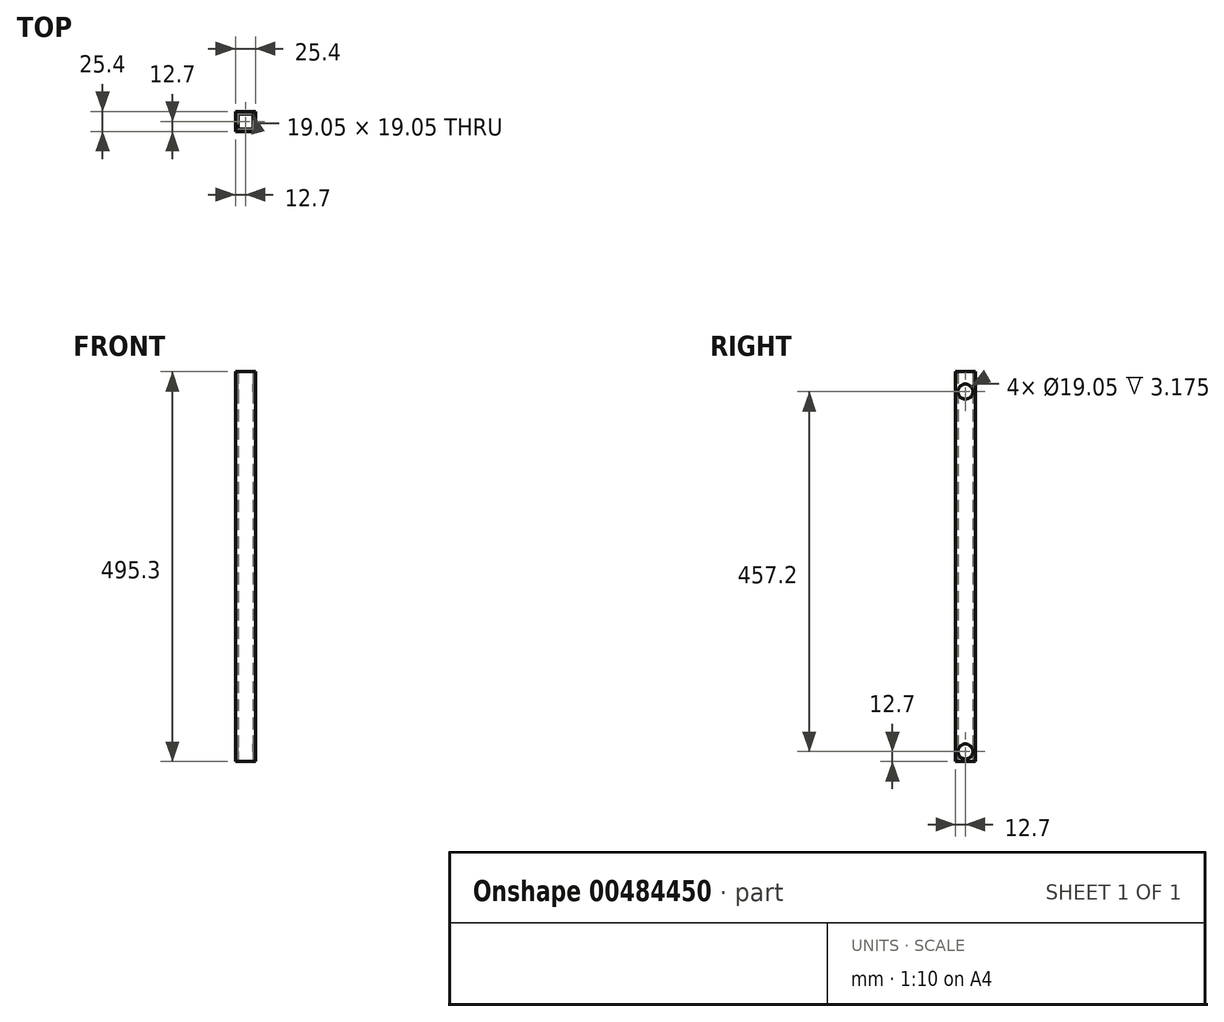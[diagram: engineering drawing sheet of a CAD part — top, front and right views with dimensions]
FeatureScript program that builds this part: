
annotation { "Feature Type Name" : "Feature", "Feature Type Description" : "" }
export const myFeature = defineFeature(function(context is Context, id is Id, definition is map)
    precondition{}
    {
        {
            var Q0;
            Q0=qCreatedBy(makeId("Top.planeOp"),FACE);
            var sketch = newSketch(context, id + "F0", { "sketchPlane" : qUnion([Q0])});
            skLineSegment(sketch, "E0.bottom", {"start": v(12.7, 12.7) * mm, "end": v(-12.7, 12.7) * mm});
            skLineSegment(sketch, "E0.top", {"start": v(12.7, -12.7) * mm, "end": v(-12.7, -12.7) * mm});
            skLineSegment(sketch, "E0.left", {"start": v(12.7, 12.7) * mm, "end": v(12.7, -12.7) * mm});
            skLineSegment(sketch, "E0.right", {"start": v(-12.7, 12.7) * mm, "end": v(-12.7, -12.7) * mm});
            skPoint(sketch, "E0.middle", {"position": v(0, 0) * mm});
            skLineSegment(sketch, "E1.0", {"start": v(9.53, 9.53) * mm, "end": v(-9.53, 9.53) * mm});
            skLineSegment(sketch, "E1.1", {"start": v(9.53, 9.53) * mm, "end": v(9.53, -9.52) * mm});
            skLineSegment(sketch, "E1.2", {"start": v(9.53, -9.52) * mm, "end": v(-9.53, -9.52) * mm});
            skLineSegment(sketch, "E1.3", {"start": v(-9.53, 9.53) * mm, "end": v(-9.53, -9.52) * mm});
            skSolve(sketch);
        }
        {
            var Q0;
            Q0=makeQuery(id+"F0.imprint","IMPRINT",FACE,{"disambiguationData":[TD([[makeQuery(id+"F0.imprint","IMPRINT",EDGE,{"derivedFrom":sQuery(id+"F0.wireOp",EDGE,"E0.bottom")}),1.0]])]});
            extrude(context, id + "F1", {"entities" : qUnion([Q0]), "depth" : 495.3 * mm});
        }
        {
            var Q0;
            Q0=makeQuery(id+"F1.opExtrude","SWEPT_FACE",FACE,{"disambiguationData":[OSD([sQuery(id+"F0.wireOp",EDGE,"E0.left")])]});
            var sketch = newSketch(context, id + "F2", { "sketchPlane" : qUnion([Q0])});
            skCircle(sketch, "E2", {"center": v(0, 469.9) * mm, "radius": 9.53 * mm});
            skPoint(sketch, "E2.centerSnap0", {"position": v(0, 495.3) * mm});
            skSolve(sketch);
        }
        {
            var Q0;
            Q0=makeQuery(id+"F2.imprint","IMPRINT",FACE,{"disambiguationData":[TD([[makeQuery(id+"F2.imprint","IMPRINT",EDGE,{"derivedFrom":sQuery(id+"F2.wireOp",EDGE,"E2")}),1.0]])]});
            extrude(context, id + "F3", {"entities" : qUnion([Q0]), "operationType" : NewBodyOperationType.REMOVE, "oppositeDirection" : true, "depth" : 25.4 * mm});
        }
        {
            var Q0;
            Q0=makeQuery(id+"F1.opExtrude","SWEPT_FACE",FACE,{"disambiguationData":[OSD([sQuery(id+"F0.wireOp",EDGE,"E0.left")])]});
            var sketch = newSketch(context, id + "F4", { "sketchPlane" : qUnion([Q0])});
            skCircle(sketch, "E3", {"center": v(0, 12.7) * mm, "radius": 9.53 * mm});
            skSolve(sketch);
        }
        {
            var Q0;
            Q0=makeQuery(id+"F4.imprint","IMPRINT",FACE,{"disambiguationData":[TD([[makeQuery(id+"F4.imprint","IMPRINT",EDGE,{"derivedFrom":sQuery(id+"F4.wireOp",EDGE,"E3")}),1.0]])]});
            extrude(context, id + "F5", {"entities" : qUnion([Q0]), "operationType" : NewBodyOperationType.REMOVE, "oppositeDirection" : true, "depth" : 25.4 * mm});
        }
    });
